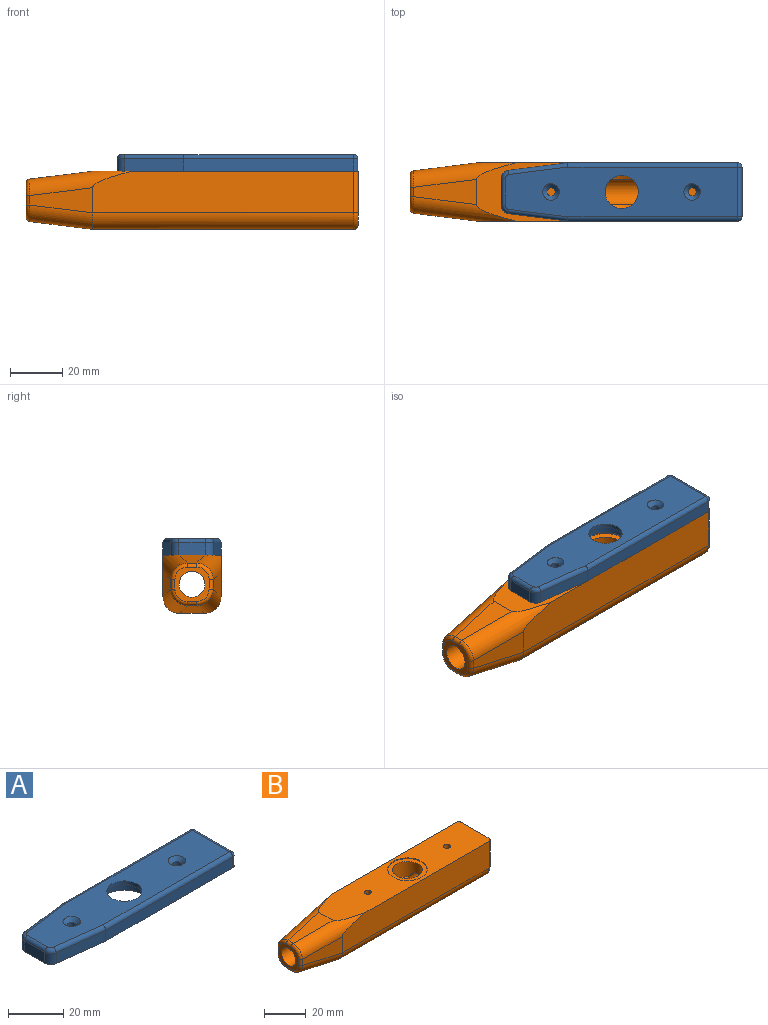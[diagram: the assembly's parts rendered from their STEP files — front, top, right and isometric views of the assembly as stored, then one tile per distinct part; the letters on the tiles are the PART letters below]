
ASSEMBLY  parts=2 mates=1
PART A: 29 faces, bbox 92.3x22.2x6.4 mm
  f0: cylinder r=6.35mm len=12.7mm, axis (0,0,-1), area 62.8mm2, adj f5,f7
  f1: plane 10.27x4.76mm, normal (-1,0,0), area 48.9mm2, adj f6,f15,f16,f25
  f2: plane 65.09x4.76mm, normal (0,-1,0), area 310mm2, adj f6,f13,f17,f18
  f3: plane 19.05x4.76mm, normal (1,0,0), area 90.7mm2, adj f6,f17,f21,f22
  f4: plane 65.09x4.76mm, normal (0,1,0), area 310mm2, adj f6,f14,f21,f26
  f5: plane 88.9x19.05mm, normal (0,0,1), area 1431.3mm2, adj f0,f10,f12,f18,f20,f22,f23,f25
  f6: plane 92.08x22.23mm, normal (0,0,-1), area 1660.6mm2, adj f1,f2,f3,f4,f8,f9,f11,f13
  f7: plane 19.05x19.05mm, normal (0,0,-1), area 158.3mm2, adj f0,f8
  f8: cylinder r=9.53mm len=19.05mm, axis (0,0,-1), area 285.8mm2, adj f6,f7
  f9: cylinder r=1.59mm len=4.76mm, axis (0,0,1), area 47.5mm2, adj f6,f10
  f10: cone r=1.59mm half-angle=45deg, axis (0,0,1), area 33.6mm2, adj f5,f9
  f11: cylinder r=1.59mm len=4.76mm, axis (0,0,1), area 47.5mm2, adj f6,f12
  f12: cone r=1.59mm half-angle=45deg, axis (0,0,1), area 33.6mm2, adj f5,f11
  f13: plane 22.62x4.76mm, normal (-0.12,-0.99,0), area 108.6mm2, adj f2,f6,f15,f20
  f14: plane 22.62x4.76mm, normal (-0.12,0.99,0), area 108.6mm2, adj f4,f6,f16,f28
  f15: cylinder r=3.17mm len=4.76mm, axis (0,0,1), area 21.9mm2, adj f1,f6,f13,f23
  f16: cylinder r=3.17mm len=4.76mm, axis (0,0,1), area 21.9mm2, adj f1,f6,f14,f27
  f17: cylinder r=1.59mm len=4.76mm, axis (0,0,-1), area 11.9mm2, adj f2,f3,f6,f19
  f18: cylinder r=1.59mm len=65.09mm, axis (-1,0,0), area 162.2mm2, adj f2,f5,f19,f20
  f19: sphere r=1.59mm, area 4mm2, adj f17,f18,f22
  f20: cylinder r=1.59mm len=22.82mm, axis (0.99,-0.12,0), area 56.8mm2, adj f5,f13,f18,f23
  f21: cylinder r=1.59mm len=4.76mm, axis (0,0,1), area 11.9mm2, adj f3,f4,f6,f24
  f22: cylinder r=1.59mm len=19.05mm, axis (0,-1,0), area 47.5mm2, adj f3,f5,f19,f24
  f23: torus R=1.59mm, axis (0,0,1), area 9.4mm2, adj f5,f15,f20,f25
  f24: sphere r=1.59mm, area 4mm2, adj f21,f22,f26
  f25: cylinder r=1.59mm len=10.27mm, axis (0,1,0), area 25.6mm2, adj f1,f5,f23,f27
  f26: cylinder r=1.59mm len=65.09mm, axis (1,0,0), area 162.2mm2, adj f4,f5,f24,f28
  f27: torus R=1.59mm, axis (0,0,1), area 9.4mm2, adj f5,f16,f25,f28
  f28: cylinder r=1.59mm len=22.82mm, axis (0.99,0.12,0), area 56.8mm2, adj f5,f14,f26,f27
PART B: 39 faces, bbox 127x26x24.6 mm
  f0: plane 20.64x19.05mm, normal (1,0,0), area 305.9mm2, adj f2,f3,f24,f25,f26,f27,f33
  f1: plane 13.07x13.07mm, normal (-1,0,0), area 74.3mm2, adj f3,f20,f21,f22,f23,f30,f32,f36
  f2: plane 101.51x22.23mm, normal (0,0,1), area 1886mm2, adj f0,f4,f5,f11,f12,f14,f16,f24
  f3: cylinder r=4.97mm len=127mm, axis (1,0,0), area 3784.6mm2, adj f0,f1,f7,f8,f9
  f4: plane 99.92x15.88mm, normal (0,-1,0), area 1552.2mm2, adj f2,f17,f26,f28,f31
  f5: plane 99.92x15.88mm, normal (0,1,0), area 1552.2mm2, adj f2,f18,f24,f34,f37
  f6: plane 99.92x9.53mm, normal (0,0,-1), area 951.8mm2, adj f19,f25,f28,f34
  f7: cylinder r=7.15mm len=14.3mm, axis (0,0,1), area 360.5mm2, adj f3,f8,f9,f10
  f8: cone r=0mm half-angle=59deg, axis (0,0,1), area 19mm2, adj f3,f7
  f9: cone r=0mm half-angle=59deg, axis (0,0,1), area 19mm2, adj f3,f7
  f10: plane 19.05x19.05mm, normal (0,0,1), area 124.4mm2, adj f7,f11
  f11: cylinder r=9.53mm len=19.05mm, axis (0,0,1), area 24.3mm2, adj f2,f10
  f12: cylinder r=1.59mm len=3.18mm, axis (0,0,1), area 31.7mm2, adj f2,f13
  f13: plane 3.18x3.18mm, normal (0,0,1), area 7.9mm2, adj f12
  f14: cylinder r=1.59mm len=3.18mm, axis (0,0,1), area 31.7mm2, adj f2,f15
  f15: plane 3.18x3.18mm, normal (0,0,1), area 7.9mm2, adj f14
  f16: plane 24.1x9.62mm, normal (-0.12,0,0.99), area 160.8mm2, adj f2,f20,f31,f37
  f17: plane 24.1x9.62mm, normal (-0.12,-0.99,0), area 160.8mm2, adj f4,f22,f28,f29,f31
  f18: plane 24.1x9.62mm, normal (-0.12,0.99,0), area 160.8mm2, adj f5,f21,f34,f35,f37
  f19: plane 24.1x9.62mm, normal (-0.12,0,-0.99), area 160.8mm2, adj f6,f23,f28,f29,f34,f35
  f20: cylinder r=1.59mm len=3.62mm, axis (0,-1,0), area 8.3mm2, adj f1,f16,f32,f38
  f21: cylinder r=1.59mm len=3.62mm, axis (0,0,-1), area 8.3mm2, adj f1,f18,f36,f38
  f22: cylinder r=1.59mm len=3.62mm, axis (0,0,-1), area 8.3mm2, adj f1,f17,f30,f32
  f23: cylinder r=1.59mm len=3.62mm, axis (0,-1,0), area 8.3mm2, adj f1,f19,f30,f36
  f24: cylinder r=1.59mm len=15.88mm, axis (0,0,-1), area 39.6mm2, adj f0,f2,f5,f33
  f25: cylinder r=1.59mm len=9.53mm, axis (0,1,0), area 23.8mm2, adj f0,f6,f27,f33
  f26: cylinder r=1.59mm len=15.88mm, axis (0,0,1), area 39.6mm2, adj f0,f2,f4,f27
  f27: torus R=4.76mm, axis (-1,0,0), area 22.6mm2, adj f0,f25,f26,f28
  f28: cylinder r=6.35mm len=100.08mm, axis (1,0,0), area 997.7mm2, adj f4,f6,f17,f19,f27,f29
  f29: cylinder r=6.35mm len=24.41mm, axis (0.98,-0.12,-0.12), area 240.1mm2, adj f17,f19,f28,f30
  f30: bspline ~6.3x6.3mm, area 20mm2, adj f1,f22,f23,f29
  f31: cylinder r=6.35mm len=39.5mm, axis (-0.98,0.12,-0.12), area 292.6mm2, adj f2,f4,f16,f17,f32
  f32: bspline ~6.63x6.63mm, area 20mm2, adj f1,f20,f22,f31
  f33: torus R=4.76mm, axis (-1,0,0), area 22.6mm2, adj f0,f24,f25,f34
  f34: cylinder r=6.35mm len=100.08mm, axis (-1,0,0), area 997.7mm2, adj f5,f6,f18,f19,f33,f35
  f35: cylinder r=6.35mm len=24.41mm, axis (0.98,0.12,-0.12), area 240.1mm2, adj f18,f19,f34,f36
  f36: bspline ~6.3x6.3mm, area 20mm2, adj f1,f21,f23,f35
  f37: cylinder r=6.35mm len=39.5mm, axis (-0.98,-0.12,-0.12), area 292.6mm2, adj f2,f5,f16,f18,f38
  f38: bspline ~6.63x6.63mm, area 20mm2, adj f1,f20,f21,f37
PLACE A t=(12.63,1.9,18.13)mm
PLACE B t=(-4.82,1.9,-4.1)mm fixed
MATE fastened A.f8 <-> B.f7  axis (0,0,-1) through (12.63,1.9,18.13)mm
